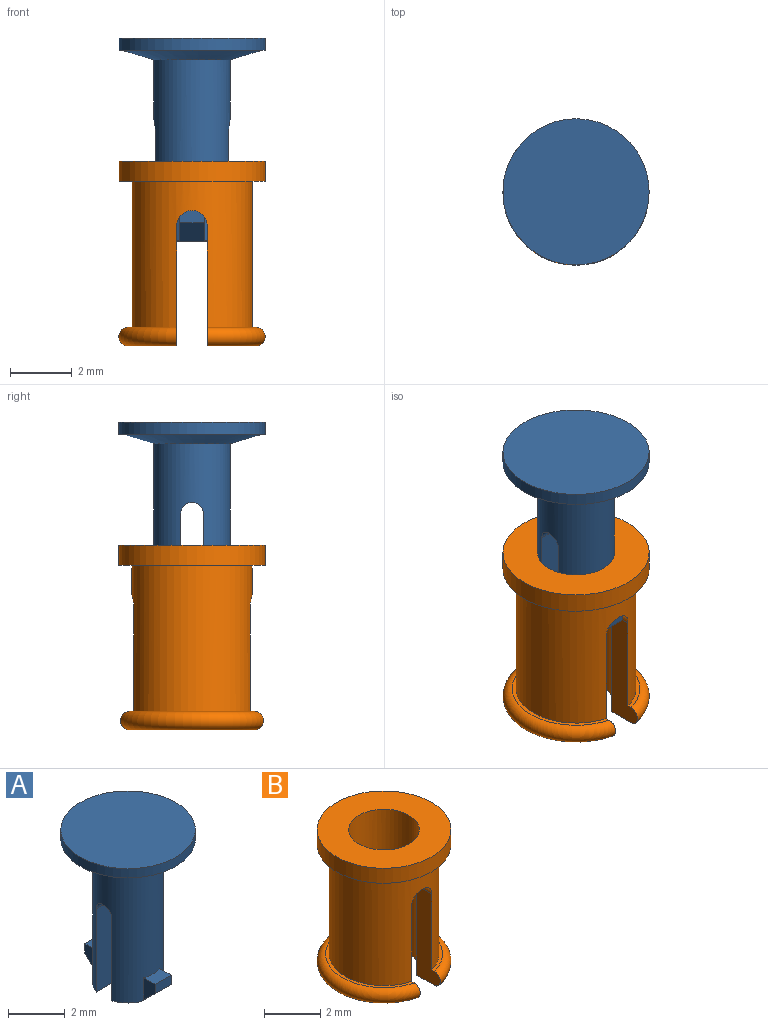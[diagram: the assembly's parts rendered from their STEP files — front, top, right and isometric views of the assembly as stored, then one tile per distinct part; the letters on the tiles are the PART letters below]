
ASSEMBLY  parts=2 mates=1
PART A: 21 faces, bbox 4.8x4.8x6.6 mm
  f0: plane 2.39x0.78mm, normal (0,0,-1), area 1.5mm2, adj f1,f16,f17
  f1: cylinder r=1.25mm len=5.9mm, axis (0,0,1), area 38.8mm2, adj f0,f2,f6,f8,f9,f10,f11,f12
  f2: plane 2.39x0.78mm, normal (0,0,-1), area 1.5mm2, adj f1,f15,f18
  f3: cylinder r=2.38mm len=4.75mm, axis (0,0,1), area 6mm2, adj f4,f5
  f4: plane 4.75x4.75mm, normal (0,0,-1), area 1.8mm2, adj f3,f6
  f5: plane 4.75x4.75mm, normal (0,0,1), area 17.7mm2, adj f3
  f6: cone r=2.25mm half-angle=73.3deg, axis (0,0,1), area 11.5mm2, adj f1,f4
  f7: plane 0.8x0.4mm, normal (0,1,0), area 0.3mm2, adj f8,f9,f10,f16
  f8: plane 0.8x0.57mm, normal (0,0,1), area 0.4mm2, adj f1,f7,f9,f10
  f9: plane 0.97x0.57mm, normal (-1,0,0), area 0.4mm2, adj f1,f7,f8,f16
  f10: plane 0.97x0.57mm, normal (1,0,0), area 0.4mm2, adj f1,f7,f8,f16
  f11: plane 0.8x0.57mm, normal (0,0,1), area 0.4mm2, adj f1,f12,f13,f14
  f12: plane 0.97x0.57mm, normal (1,0,0), area 0.4mm2, adj f1,f11,f14,f15
  f13: plane 0.97x0.57mm, normal (-1,0,0), area 0.4mm2, adj f1,f11,f14,f15
  f14: plane 0.8x0.4mm, normal (0,-1,0), area 0.3mm2, adj f11,f12,f13,f15
  f15: plane 0.98x0.6mm, normal (0,-0.71,-0.71), area 0.7mm2, adj f1,f2,f12,f13,f14
  f16: plane 0.98x0.6mm, normal (0,0.71,-0.71), area 0.7mm2, adj f0,f1,f7,f9,f10
  f17: plane 3.6x2.39mm, normal (0,-1,0), area 8.6mm2, adj f0,f1,f19
  f18: plane 3.6x2.39mm, normal (0,1,0), area 8.6mm2, adj f1,f2,f20
  f19: cylinder r=0.4mm len=2.5mm, axis (1,0,0), area 1.5mm2, adj f1,f17,f20
  f20: cylinder r=0.4mm len=2.5mm, axis (-1,0,0), area 1.5mm2, adj f1,f18,f19
PART B: 17 faces, bbox 5.1x5x6 mm
  f0: plane 4.03x1.58mm, normal (0,0,-1), area 3.5mm2, adj f4,f10,f11,f15
  f1: plane 4.03x1.58mm, normal (0,0,1), area 0.7mm2, adj f2,f3,f12,f16
  f2: torus R=2.08mm, axis (0,0,-1), area 5.8mm2, adj f1,f5,f12,f16
  f3: cylinder r=1.95mm len=4.75mm, axis (0,0,1), area 50.7mm2, adj f1,f8,f9,f11,f12,f13,f14,f15
  f4: cylinder r=1.25mm len=6mm, axis (0,0,1), area 38.3mm2, adj f0,f5,f6,f11,f12,f13,f14,f15
  f5: plane 4.03x1.58mm, normal (0,0,-1), area 3.5mm2, adj f2,f4,f12,f16
  f6: plane 4.75x4.75mm, normal (0,0,1), area 12.8mm2, adj f4,f7
  f7: cylinder r=2.38mm len=4.75mm, axis (0,0,1), area 9.7mm2, adj f6,f8
  f8: plane 4.75x4.75mm, normal (0,0,-1), area 5.8mm2, adj f3,f7
  f9: plane 4.03x1.58mm, normal (0,0,1), area 0.7mm2, adj f3,f10,f11,f15
  f10: torus R=2.08mm, axis (0,0,-1), area 5.8mm2, adj f0,f9,f11,f15
  f11: plane 3.9x1.18mm, normal (-1,0,0), area 3.1mm2, adj f0,f3,f4,f9,f10,f13
  f12: plane 3.9x1.18mm, normal (1,0,0), area 3.1mm2, adj f1,f2,f3,f4,f5,f13
  f13: cylinder r=0.5mm len=1mm, axis (0,-1,0), area 1.1mm2, adj f3,f4,f11,f12
  f14: cylinder r=0.5mm len=1mm, axis (0,-1,0), area 1.1mm2, adj f3,f4,f15,f16
  f15: plane 3.9x1.18mm, normal (-1,0,0), area 3.1mm2, adj f0,f3,f4,f9,f10,f14
  f16: plane 3.9x1.18mm, normal (1,0,0), area 3.1mm2, adj f1,f2,f3,f4,f5,f14
PLACE A t=(0,0,3.4)mm
PLACE B at identity
MATE slider A.f1 <-> B.f2  axis (0,0,1) through (0,0,-2.6)mm
